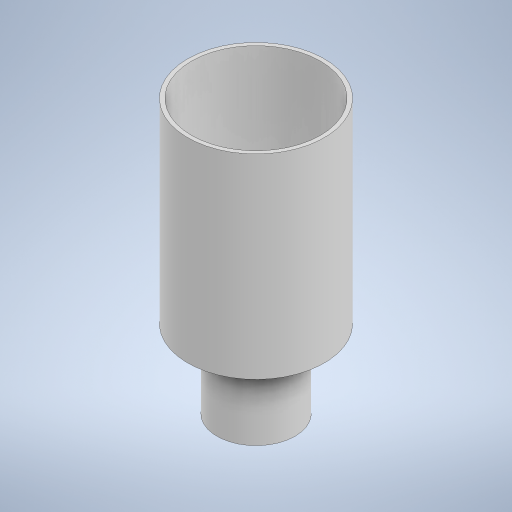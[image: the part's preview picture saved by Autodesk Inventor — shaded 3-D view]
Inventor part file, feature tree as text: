
AUTODESK INVENTOR PART (.ipt)
format: ipt  version: 2023 (Build 270158000, 158)  size: 244,736 bytes
history: native  units: in
note: dims shown in document units (in); Inventor stores cm internally (conversion verified against a paired STEP export)
features: sketch x2, extrude x2, shell x1, hole x1
ambient origin geometry x8: Origin, YZ Plane, XZ Plane, XY Plane, X Axis, Y Axis, Z Axis, Center Point
bodies: Solid1 (feature_tree)
feature tree (6):
  sketch  "Sketch1"  dims[d0=1.378in d1=0.7874in]
  extrude  "Extrusion1"  Depth=0.7874in
  extrude  "Extrusion2"  Depth=0.7874in TaperAngle=0.0deg
  shell  "Shell1"  Thickness=0.0394in
  hole  "Hole1"  [1 undecoded]
  sketch  "Sketch2"  dims[d2=1.9685in d3=0.0in d4=0.7874in d5=0.0in d6=0.0394in d8=0.7677in d9=0.2362in d10=0.1575in d11=0.0787in d12=90.0deg d13=1.9685in d14=0.0in d15=0.0197in d16=0.0344in d17=0.0197in d18=0.0344in]
note: 1 required parameter value undecoded (feature->parameter linkage not recoverable at this tier; creation-order binding heuristic only, values carry confidence <= 0.55)
